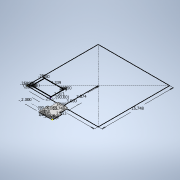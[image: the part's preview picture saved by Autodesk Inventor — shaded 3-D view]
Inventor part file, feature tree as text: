
AUTODESK INVENTOR PART (.ipt)
format: ipt  version: 2020 (Build 240168000, 168)  size: 312,320 bytes
history: native  units: in
note: dims shown in document units (in); Inventor stores cm internally (conversion verified against a paired STEP export)
features: sketch x6, extrude x6, hole x3, fillet x2, pattern_linear x1
ambient origin geometry x8: Origin, YZ Plane, XZ Plane, XY Plane, X Axis, Y Axis, Z Axis, Center Point
bodies: Solid1 (feature_tree)
feature tree (18):
  sketch  "Sketch1"  dims[d0=3.0in d1=2.0in]
  extrude  "Extrusion1"  Depth=3.0in
  hole  "Hole1"  [1 undecoded]
  sketch  "Sketch2"  dims[d2=0.25in d3=1.0in]
  extrude  "Extrusion2"  TaperAngle=0.0deg  [1 undecoded]
  hole  "Hole2"  [1 undecoded]
  extrude  "Extrusion3"  Depth=0.25in
  pattern_linear  "Rectangular Pattern1"  Spacing1=90.0deg  [1 undecoded]
  extrude  "Extrusion4"  Depth=0.125in
  extrude  "Extrusion5"  Depth=0.125in
  hole  "Hole3"  [1 undecoded]
  extrude  "Extrusion6"  TaperAngle=90.0deg  [1 undecoded]
  fillet  "Fillet1"  Radius=15.748in
  fillet  "Fillet2"  Radius=15.748in
  sketch  "Sketch3"  dims[d4=1.0in d5=0.0in]
  sketch  "Sketch4"  dims[d6=0.5in d7=0.5in]
  sketch  "Sketch5"  dims[d8=0.25in d9=0.25in]
  sketch  "Sketch6"  dims[d10=2.9528in d11=90.0deg d12=2.9528in d13=1.0in d14=7.874in d15=90.0deg d16=15.748in d17=15.748in d18=0.25in d19=0.0in d20=0.26in d21=0.5in d22=0.375in d23=0.25in d24=0.5635in d25=1.0in d26=0.8108in d27=0.25in d28=90.0deg d29=0.25in d30=0.25in d31=0.25in d32=4.3386in d33=2.9134in d34=0.25in d35=0.25in d36=0.25in d37=0.25in d38=0.25in d39=0.315in d40=90.0deg d41=0.0787in d42=0.0787in d43=0.0787in d44=0.0787in d45=0.0in d46=0.0in d47=0.203in d48=0.625in d49=0.375in d50=0.25in d51=0.5635in d52=1.0in d53=0.8108in d54=0.0787in d55=0.0in d56=1.1811in d58=4.839in d59=1.5748in d61=3.423in d62=0.25in d63=0.25in d64=0.0in d65=0.0in d66=1.0in d67=0.0in d68=0.25in d69=0.5in d70=90.0deg d71=1.0in d72=0.266in d73=0.75in d74=0.438in d75=0.25in d76=0.5635in d77=1.0in d78=0.8108in d79=1.5in d80=0.125in d81=0.125in d82=0.0in d83=0.125in d84=0.125in]
note: 6 required parameter values undecoded (feature->parameter linkage not recoverable at this tier; creation-order binding heuristic only, values carry confidence <= 0.55)
